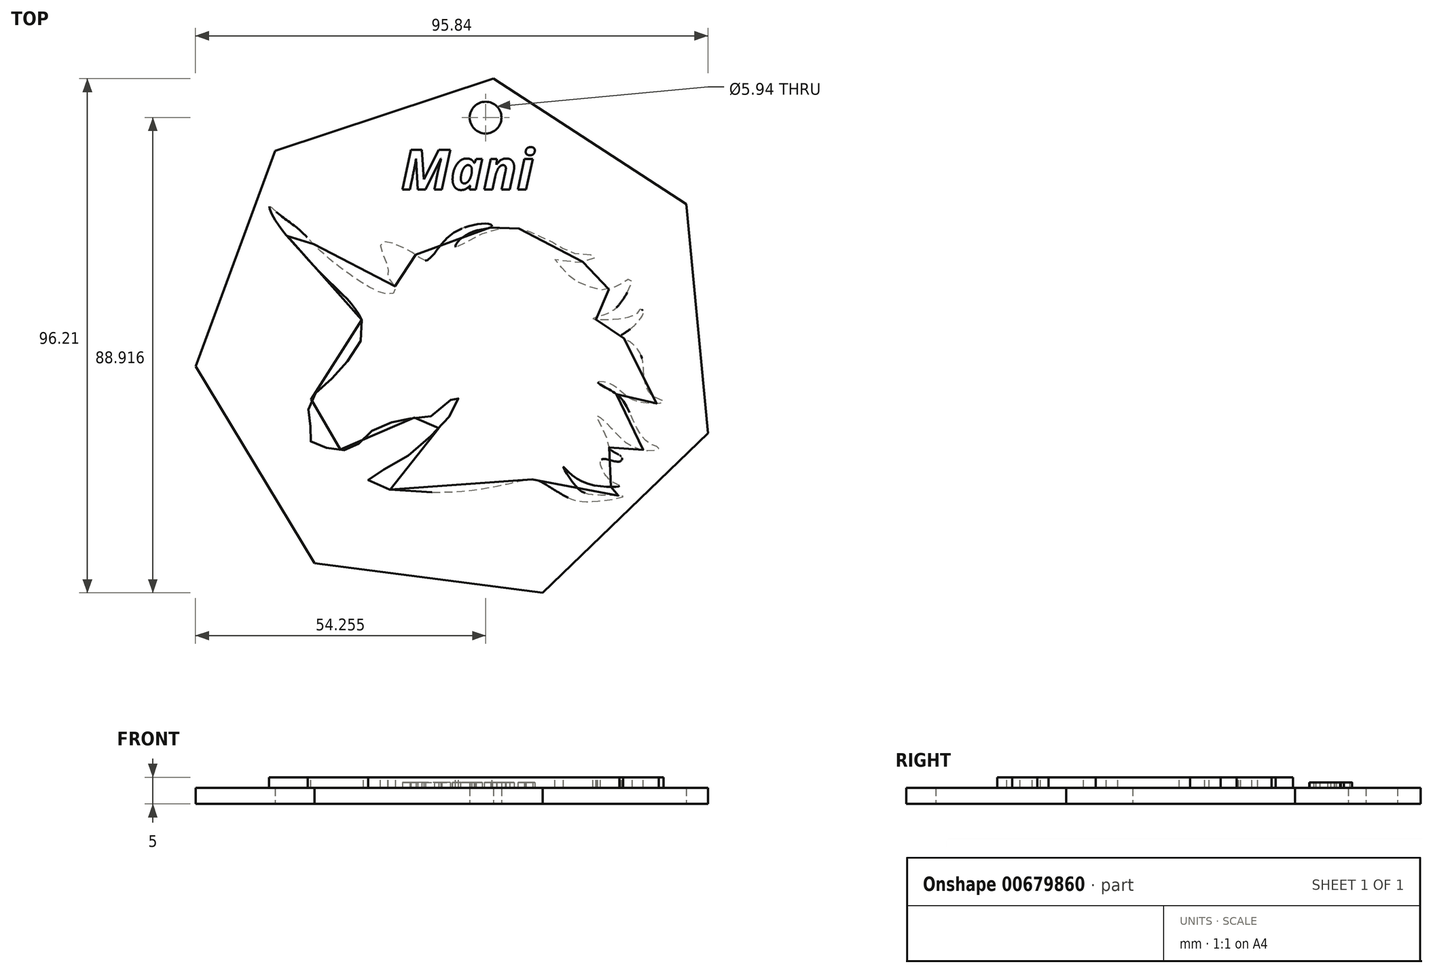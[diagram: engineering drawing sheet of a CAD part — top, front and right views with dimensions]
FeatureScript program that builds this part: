
annotation { "Feature Type Name" : "Feature", "Feature Type Description" : "" }
export const myFeature = defineFeature(function(context is Context, id is Id, definition is map)
    precondition{}
    {
        {
            var Q0;
            Q0=qCreatedBy(makeId("Top.planeOp"),FACE);
            var sketch = newSketch(context, id + "F0", { "sketchPlane" : qUnion([Q0])});
            skFitSpline(sketch, "E0", {"points": [v(-56.48, 43.47) * mm, v(-56.48, 40.02) * mm, v(-58.76, 36.24) * mm, v(-61.6, 32.96) * mm, v(-64.54, 30.3) * mm, v(-66.15, 28.18) * mm, v(-66.32, 25.74) * mm, v(-66.04, 23.52) * mm, v(-66.54, 21.85) * mm, v(-64.93, 19.85) * mm, v(-62.87, 19.51) * mm, v(-60.54, 19.24) * mm, v(-57.98, 19.3) * mm, v(-56.6, 20.96) * mm, v(-54.48, 22.8) * mm, v(-51.15, 24.24) * mm, v(-48.64, 24.74) * mm, v(-45.2, 25.35) * mm, v(-41.92, 26.07) * mm, v(-38.64, 29.8) * mm, v(-38.36, 29.13) * mm, v(-39.25, 26.63) * mm, v(-42.2, 23.07) * mm, v(-47.31, 18.4) * mm, v(-52.7, 15.3) * mm, v(-55.2, 13.73) * mm, v(-54.15, 12.46) * mm, v(-42.36, 11.23) * mm, v(-33.92, 11.9) * mm, v(-27.25, 13.23) * mm, v(-24.13, 13.62) * mm, v(-21.86, 12.57) * mm, v(-18.47, 10.51) * mm, v(-14.24, 9.46) * mm, v(-7.57, 10.46) * mm, v(-11.9, 10.68) * mm, v(-16.13, 12.07) * mm, v(-18.74, 15.96) * mm, v(-15.35, 13.29) * mm, v(-8.24, 12.4) * mm, v(-10.07, 13.57) * mm, v(-11.63, 17.35) * mm, v(-8.4, 16.96) * mm, v(-7.8, 17.74) * mm, v(-9.85, 19.13) * mm, v(-10.57, 21.24) * mm, v(-12.46, 25.52) * mm, v(-10.85, 24.35) * mm, v(-8.74, 22.13) * mm, v(-6.13, 19.96) * mm, v(-2.07, 19.01) * mm, v(-0.9, 19.51) * mm, v(-2.4, 20.24) * mm, v(-4.68, 22.68) * mm, v(-6.68, 26.85) * mm, v(-8.4, 29.24) * mm, v(-11.35, 31.13) * mm, v(-12.3, 31.85) * mm, v(-10.24, 31.69) * mm, v(-7.35, 29.63) * mm, v(-5.07, 28.3) * mm, v(-0.74, 27.9) * mm, v(0, 28.24) * mm, v(-2.01, 29.3) * mm, v(-3.63, 32.46) * mm, v(-3.96, 35.97) * mm, v(-5.85, 39.02) * mm, v(-7.9, 40.47) * mm, v(-6.85, 41.3) * mm, v(-3.8, 44.91) * mm, v(-4.35, 45.47) * mm, v(-4.9, 44.8) * mm, v(-8.74, 43.58) * mm, v(-13.19, 43.7) * mm, v(-10.63, 44.64) * mm, v(-8.07, 46.64) * mm, v(-6.02, 50.2) * mm, v(-5.96, 51.2) * mm, v(-9.85, 49.3) * mm, v(-13.35, 49.53) * mm, v(-16.8, 50.97) * mm, v(-18.58, 52.75) * mm, v(-20.32, 54.87) * mm, v(-16.84, 54.23) * mm, v(-12.66, 55.35) * mm, v(-16.49, 55.88) * mm, v(-20.08, 57.58) * mm, v(-23.55, 59.3) * mm, v(-27.09, 60.59) * mm, v(-34.21, 59.47) * mm, v(-38.86, 57.05) * mm, v(-38.63, 57.94) * mm, v(-35.04, 60.17) * mm, v(-32.1, 60.94) * mm, v(-32.39, 61.35) * mm, v(-36.69, 60.94) * mm, v(-41.1, 58.17) * mm, v(-44.28, 54.64) * mm, v(-45.93, 55.35) * mm, v(-49.46, 57.35) * mm, v(-52.7, 58) * mm, v(-52.64, 56.05) * mm, v(-51.52, 52.99) * mm, v(-51.46, 51.22) * mm, v(-50.17, 49.57) * mm, v(-50.76, 48.34) * mm, v(-53.11, 48.7) * mm, v(-57.18, 50.93) * mm, v(-62.77, 55.1) * mm, v(-66.07, 58.29) * mm, v(-68.42, 60.59) * mm, v(-72.07, 63.39) * mm, v(-73.75, 64.7) * mm, v(-72.52, 61.94) * mm, v(-69.92, 58.61) * mm, v(-66.22, 54.47) * mm, v(-62.02, 50.15) * mm, v(-59.1, 47.27) * mm, v(-56.48, 43.47) * mm]});
            skSolve(sketch);
        }
        {
            var Q0;
            Q0=makeQuery(id+"F0.imprint","IMPRINT",FACE,{"disambiguationData":[TD([[makeQuery(id+"F0.imprint","IMPRINT",EDGE,{"derivedFrom":sQuery(id+"F0.wireOp",EDGE,"E0")}),1.0]])]});
            extrude(context, id + "F1", {"entities" : qUnion([Q0]), "depth" : 5 * mm, "offsetDistance" : 25.4 * mm});
        }
        {
            var Q0;
            Q0=qCreatedBy(makeId("Top.planeOp"),FACE);
            var sketch = newSketch(context, id + "F2", { "sketchPlane" : qUnion([Q0])});
            skCircle(sketch, "E1.cCircle", {"center": v(-38.2, 39.47) * mm, "radius": 44.66 * mm, "construction": true});
            skLineSegment(sketch, "E1.0", {"start": v(8.3, 22.3) * mm, "end": v(-22.63, -7.6) * mm});
            skLineSegment(sketch, "E1.1", {"start": v(-22.63, -7.6) * mm, "end": v(-65.29, -2.04) * mm});
            skLineSegment(sketch, "E1.2", {"start": v(-65.29, -2.04) * mm, "end": v(-87.54, 34.77) * mm});
            skLineSegment(sketch, "E1.3", {"start": v(-87.54, 34.77) * mm, "end": v(-72.63, 75.11) * mm});
            skLineSegment(sketch, "E1.4", {"start": v(-72.63, 75.11) * mm, "end": v(-31.8, 88.62) * mm});
            skLineSegment(sketch, "E1.5", {"start": v(-31.8, 88.62) * mm, "end": v(4.22, 65.1) * mm});
            skLineSegment(sketch, "E1.6", {"start": v(4.22, 65.1) * mm, "end": v(8.3, 22.3) * mm});
            skPoint(sketch, "E1.0.midPoint", {"position": v(-7.17, 7.35) * mm});
            skCircle(sketch, "E2", {"center": v(-33.29, 81.33) * mm, "radius": 2.97 * mm});
            skSolve(sketch);
        }
        {
            var Q0;
            Q0=makeQuery(id+"F2.imprint","IMPRINT",FACE,{"disambiguationData":[TD([[makeQuery(id+"F2.imprint","IMPRINT",EDGE,{"derivedFrom":sQuery(id+"F2.wireOp",EDGE,"E1.0")}),-1.0]])]});
            extrude(context, id + "F3", {"entities" : qUnion([Q0]), "operationType" : NewBodyOperationType.ADD, "depth" : 3 * mm, "offsetDistance" : 25 * mm});
        }
        {
            var Q0;
            Q0=qCreatedBy(makeId("Top.planeOp"),FACE);
            var sketch = newSketch(context, id + "F4", { "sketchPlane" : qUnion([Q0])});
            skText(sketch, "E3", { "text": "Mani", "fontName": "OpenSans-BoldItalic.ttf"});
            const initialGuessF4  = {"E3": [-0.04912, 0.06787, 1, 0, 0.00752]};
            skSetInitialGuess(sketch, initialGuessF4);
            skSolve(sketch);
        }
        {
            var Q0;
            Q0 = qSketchRegion(id + "F4", true);
            extrude(context, id + "F5", {"entities" : qUnion([Q0]), "operationType" : NewBodyOperationType.ADD, "depth" : 4 * mm, "offsetDistance" : 25 * mm});
        }
    });
